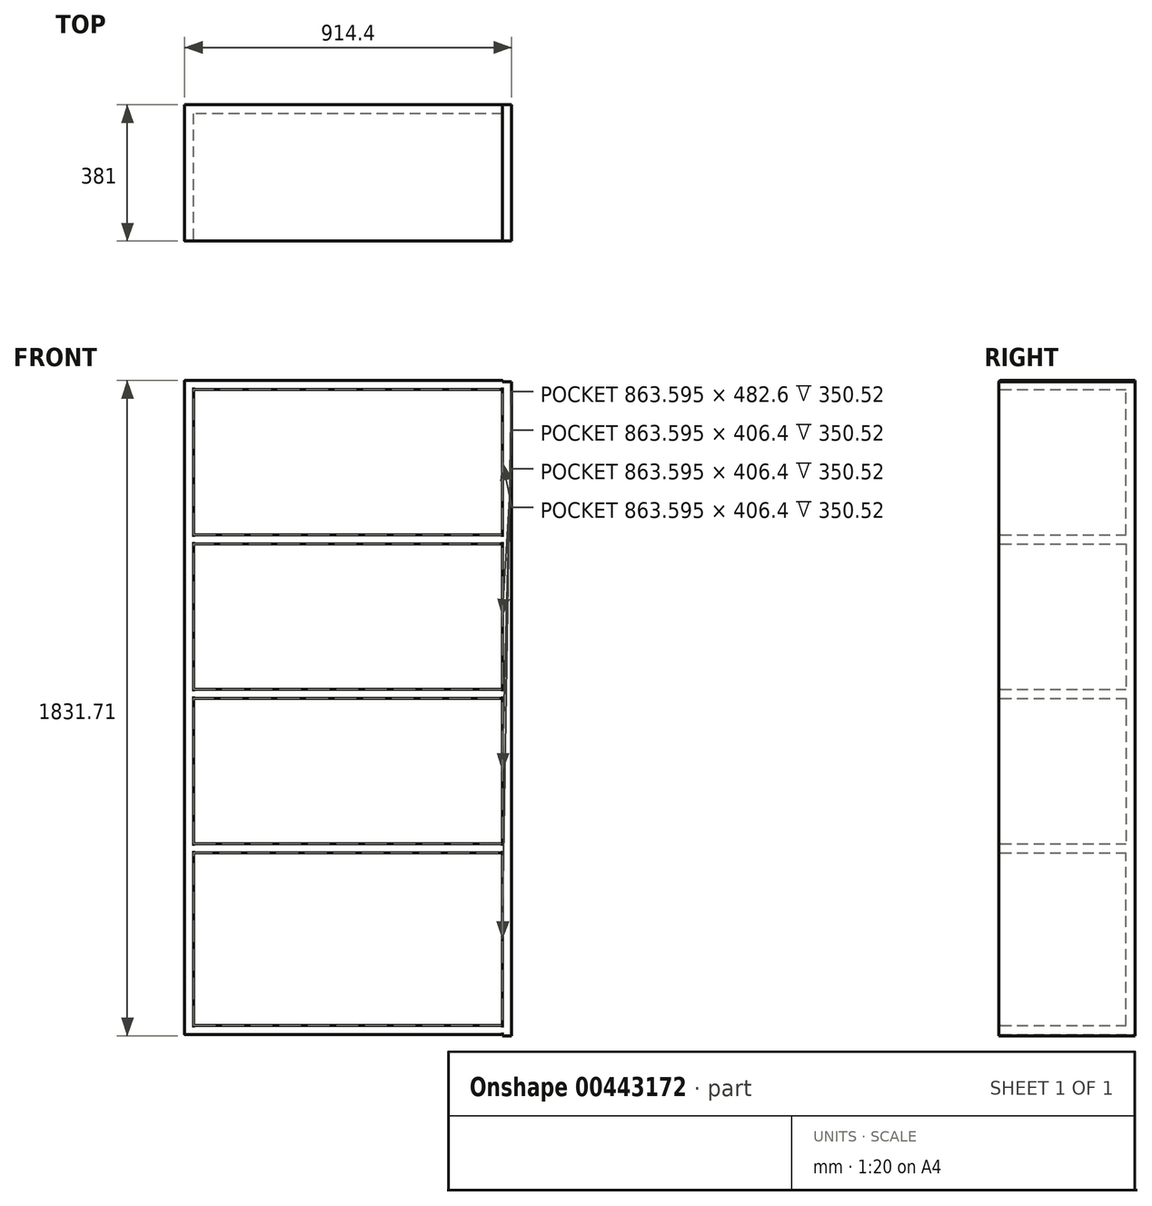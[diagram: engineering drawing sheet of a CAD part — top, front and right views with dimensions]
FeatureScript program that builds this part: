
annotation { "Feature Type Name" : "Feature", "Feature Type Description" : "" }
export const myFeature = defineFeature(function(context is Context, id is Id, definition is map)
    precondition{}
    {
        {
            var Q0;
            Q0=qCreatedBy(makeId("Front.planeOp"),FACE);
            var sketch = newSketch(context, id + "F0", { "sketchPlane" : qUnion([Q0])});
            skLineSegment(sketch, "E0.bottom", {"start": v(-12.7, -914.4) * mm, "end": v(12.7, -914.4) * mm});
            skLineSegment(sketch, "E0.top", {"start": v(-12.7, 914.4) * mm, "end": v(12.7, 914.4) * mm});
            skLineSegment(sketch, "E0.left", {"start": v(-12.7, -914.4) * mm, "end": v(-12.7, 914.4) * mm});
            skLineSegment(sketch, "E0.right", {"start": v(12.7, -914.4) * mm, "end": v(12.7, 914.4) * mm});
            skPoint(sketch, "E0.middle", {"position": v(0, 0) * mm});
            skLineSegment(sketch, "E1.bottom", {"start": v(-901.7, 917.31) * mm, "end": v(-876.3, 917.31) * mm});
            skLineSegment(sketch, "E1.top", {"start": v(-901.7, -911.49) * mm, "end": v(-876.3, -911.49) * mm});
            skLineSegment(sketch, "E1.left", {"start": v(-901.7, 917.31) * mm, "end": v(-901.7, -911.49) * mm});
            skLineSegment(sketch, "E1.right", {"start": v(-876.3, 917.31) * mm, "end": v(-876.3, -911.49) * mm});
            skLineSegment(sketch, "E2.bottom", {"start": v(-876.3, 917.31) * mm, "end": v(-12.7, 917.31) * mm});
            skLineSegment(sketch, "E2.top", {"start": v(-876.3, 891.91) * mm, "end": v(-12.7, 891.91) * mm});
            skLineSegment(sketch, "E2.left", {"start": v(-876.3, 917.31) * mm, "end": v(-876.3, 891.91) * mm});
            skLineSegment(sketch, "E2.right", {"start": v(-12.7, 917.31) * mm, "end": v(-12.7, 891.91) * mm});
            skLineSegment(sketch, "E3.bottom", {"start": v(-876.3, -911.49) * mm, "end": v(-12.7, -911.49) * mm});
            skLineSegment(sketch, "E3.top", {"start": v(-876.3, -886.09) * mm, "end": v(-12.7, -886.09) * mm});
            skLineSegment(sketch, "E3.left", {"start": v(-876.3, -911.49) * mm, "end": v(-876.3, -886.09) * mm});
            skLineSegment(sketch, "E3.right", {"start": v(-12.7, -911.49) * mm, "end": v(-12.7, -886.09) * mm});
            skLineSegment(sketch, "E4.bottom", {"start": v(-876.3, 485.51) * mm, "end": v(-12.7, 485.51) * mm});
            skLineSegment(sketch, "E4.top", {"start": v(-876.3, 460.11) * mm, "end": v(-12.7, 460.11) * mm});
            skLineSegment(sketch, "E4.left", {"start": v(-876.3, 485.51) * mm, "end": v(-876.3, 460.11) * mm});
            skLineSegment(sketch, "E4.right", {"start": v(-12.7, 485.51) * mm, "end": v(-12.7, 460.11) * mm});
            skLineSegment(sketch, "E5.bottom", {"start": v(-12.7, 53.71) * mm, "end": v(-876.3, 53.71) * mm});
            skLineSegment(sketch, "E5.top", {"start": v(-12.7, 28.31) * mm, "end": v(-876.3, 28.31) * mm});
            skLineSegment(sketch, "E5.left", {"start": v(-12.7, 53.71) * mm, "end": v(-12.7, 28.31) * mm});
            skLineSegment(sketch, "E5.right", {"start": v(-876.3, 53.71) * mm, "end": v(-876.3, 28.31) * mm});
            skLineSegment(sketch, "E6.bottom", {"start": v(-876.3, -378.09) * mm, "end": v(-12.7, -378.09) * mm});
            skLineSegment(sketch, "E6.top", {"start": v(-876.3, -403.49) * mm, "end": v(-12.7, -403.49) * mm});
            skLineSegment(sketch, "E6.left", {"start": v(-876.3, -378.09) * mm, "end": v(-876.3, -403.49) * mm});
            skLineSegment(sketch, "E6.right", {"start": v(-12.7, -378.09) * mm, "end": v(-12.7, -403.49) * mm});
            skLineSegment(sketch, "E7.left", {"start": v(-876.3, -886.09) * mm, "end": v(-876.3, 891.91) * mm});
            skLineSegment(sketch, "E7.right", {"start": v(-12.7, -886.09) * mm, "end": v(-12.7, 891.91) * mm});
            skSolve(sketch);
        }
        {
            var Q0;
            {var subQ2=sQuery(id+"F0.wireOp",EDGE,"E2.bottom");Q0=makeQuery(id+"F0.imprint","IMPRINT",FACE,{"disambiguationData":[TD([[makeQuery(id+"F0.imprint","IMPRINT",EDGE,{"derivedFrom":subQ2}),-1.0]])]});}
            var Q1;
            Q1=makeQuery(id+"F0.imprint","IMPRINT",FACE,{"disambiguationData":[TD([[makeQuery(id+"F0.imprint","IMPRINT",EDGE,{"derivedFrom":sQuery(id+"F0.wireOp",EDGE,"E3.bottom")}),1.0]])]});
            var Q2;
            Q2=makeQuery(id+"F0.imprint","IMPRINT",FACE,{"disambiguationData":[TD([[makeQuery(id+"F0.imprint","IMPRINT",EDGE,{"derivedFrom":sQuery(id+"F0.wireOp",EDGE,"E1.bottom")}),-1.0]])]});
            var Q3;
            {var subQ7=sQuery(id+"F0.wireOp",EDGE,"E0.bottom");Q3=makeQuery(id+"F0.imprint","IMPRINT",FACE,{"disambiguationData":[TD([[makeQuery(id+"F0.imprint","IMPRINT",EDGE,{"derivedFrom":subQ7}),1.0]])]});}
            var Q4;
            Q4=makeQuery(id+"F0.imprint","IMPRINT",FACE,{"disambiguationData":[TD([[makeQuery(id+"F0.imprint","IMPRINT",EDGE,{"derivedFrom":sQuery(id+"F0.wireOp",EDGE,"E4.bottom")}),-1.0]])]});
            var Q5;
            Q5=makeQuery(id+"F0.imprint","IMPRINT",FACE,{"disambiguationData":[TD([[makeQuery(id+"F0.imprint","IMPRINT",EDGE,{"derivedFrom":sQuery(id+"F0.wireOp",EDGE,"E5.bottom")}),1.0]])]});
            var Q6;
            Q6=makeQuery(id+"F0.imprint","IMPRINT",FACE,{"disambiguationData":[TD([[makeQuery(id+"F0.imprint","IMPRINT",EDGE,{"derivedFrom":sQuery(id+"F0.wireOp",EDGE,"E6.bottom")}),-1.0]])]});
            extrude(context, id + "F1", {"entities" : qUnion([Q0, Q1, Q2, Q3, Q4, Q5, Q6]), "depth" : 381 * mm});
        }
        {
            var Q0;
            Q0=makeQuery(id+"F1.opExtrude","CAP_EDGE",EDGE,{"disambiguationData":[OSD([sQuery(id+"F0.wireOp",EDGE,"E2.top")])],"isStart":false});
            var Q1;
            Q1=makeQuery(id+"F1.opExtrude","CAP_EDGE",EDGE,{"disambiguationData":[OSD([sQuery(id+"F0.wireOp",EDGE,"E1.bottom"),sQuery(id+"F0.wireOp",EDGE,"E2.bottom")])],"isStart":false});
            var Q2;
            Q2=makeQuery(id+"F1.opExtrude","CAP_EDGE",EDGE,{"disambiguationData":[OSD([sQuery(id+"F0.wireOp",EDGE,"E4.bottom")])],"isStart":false});
            var Q3;
            Q3=makeQuery(id+"F1.opExtrude","CAP_EDGE",EDGE,{"disambiguationData":[OSD([sQuery(id+"F0.wireOp",EDGE,"E4.top")])],"isStart":false});
            var Q4;
            Q4=makeQuery(id+"F1.opExtrude","CAP_EDGE",EDGE,{"disambiguationData":[OSD([sQuery(id+"F0.wireOp",EDGE,"E5.bottom")])],"isStart":false});
            var Q5;
            Q5=makeQuery(id+"F1.opExtrude","CAP_EDGE",EDGE,{"disambiguationData":[OSD([sQuery(id+"F0.wireOp",EDGE,"E6.bottom")])],"isStart":false});
            var Q6;
            Q6=makeQuery(id+"F1.opExtrude","CAP_EDGE",EDGE,{"disambiguationData":[OSD([sQuery(id+"F0.wireOp",EDGE,"E5.top")])],"isStart":false});
            var Q7;
            Q7=makeQuery(id+"F1.opExtrude","CAP_EDGE",EDGE,{"disambiguationData":[OSD([sQuery(id+"F0.wireOp",EDGE,"E6.top")])],"isStart":false});
            var Q8;
            Q8=makeQuery(id+"F1.opExtrude","CAP_EDGE",EDGE,{"disambiguationData":[OSD([sQuery(id+"F0.wireOp",EDGE,"E3.top")])],"isStart":false});
            var Q9;
            Q9=makeQuery(id+"F1.opExtrude","CAP_EDGE",EDGE,{"disambiguationData":[OSD([sQuery(id+"F0.wireOp",EDGE,"E1.top"),sQuery(id+"F0.wireOp",EDGE,"E3.bottom")])],"isStart":false});
            fillet(context, id + "F2", {"entities" : qUnion([Q0, Q1, Q2, Q3, Q4, Q5, Q6, Q7, Q8, Q9]), "radius" : 5.08 * mm, "tangentPropagation" : true, "allowEdgeOverflow" : false});
        }
        {
            var Q0;
            {var subQ0=sQuery(id+"F0.wireOp",EDGE,"E6.top");Q0=makeQuery(id+"F0.imprint","IMPRINT",FACE,{"disambiguationData":[TD([[makeQuery(id+"F0.imprint","IMPRINT",EDGE,{"derivedFrom":subQ0}),-1.0]])]});}
            var Q1;
            {var subQ0=sQuery(id+"F0.wireOp",EDGE,"E5.top");Q1=makeQuery(id+"F0.imprint","IMPRINT",FACE,{"disambiguationData":[TD([[makeQuery(id+"F0.imprint","IMPRINT",EDGE,{"derivedFrom":subQ0}),1.0]])]});}
            var Q2;
            {var subQ0=sQuery(id+"F0.wireOp",EDGE,"E4.top");Q2=makeQuery(id+"F0.imprint","IMPRINT",FACE,{"disambiguationData":[TD([[makeQuery(id+"F0.imprint","IMPRINT",EDGE,{"derivedFrom":subQ0}),-1.0]])]});}
            var Q3;
            {var subQ0=sQuery(id+"F0.wireOp",EDGE,"E4.bottom");Q3=makeQuery(id+"F0.imprint","IMPRINT",FACE,{"disambiguationData":[TD([[makeQuery(id+"F0.imprint","IMPRINT",EDGE,{"derivedFrom":subQ0}),1.0]])]});}
            extrude(context, id + "F3", {"entities" : qUnion([Q0, Q1, Q2, Q3]), "operationType" : NewBodyOperationType.ADD, "depth" : 25.4 * mm});
        }
    });
